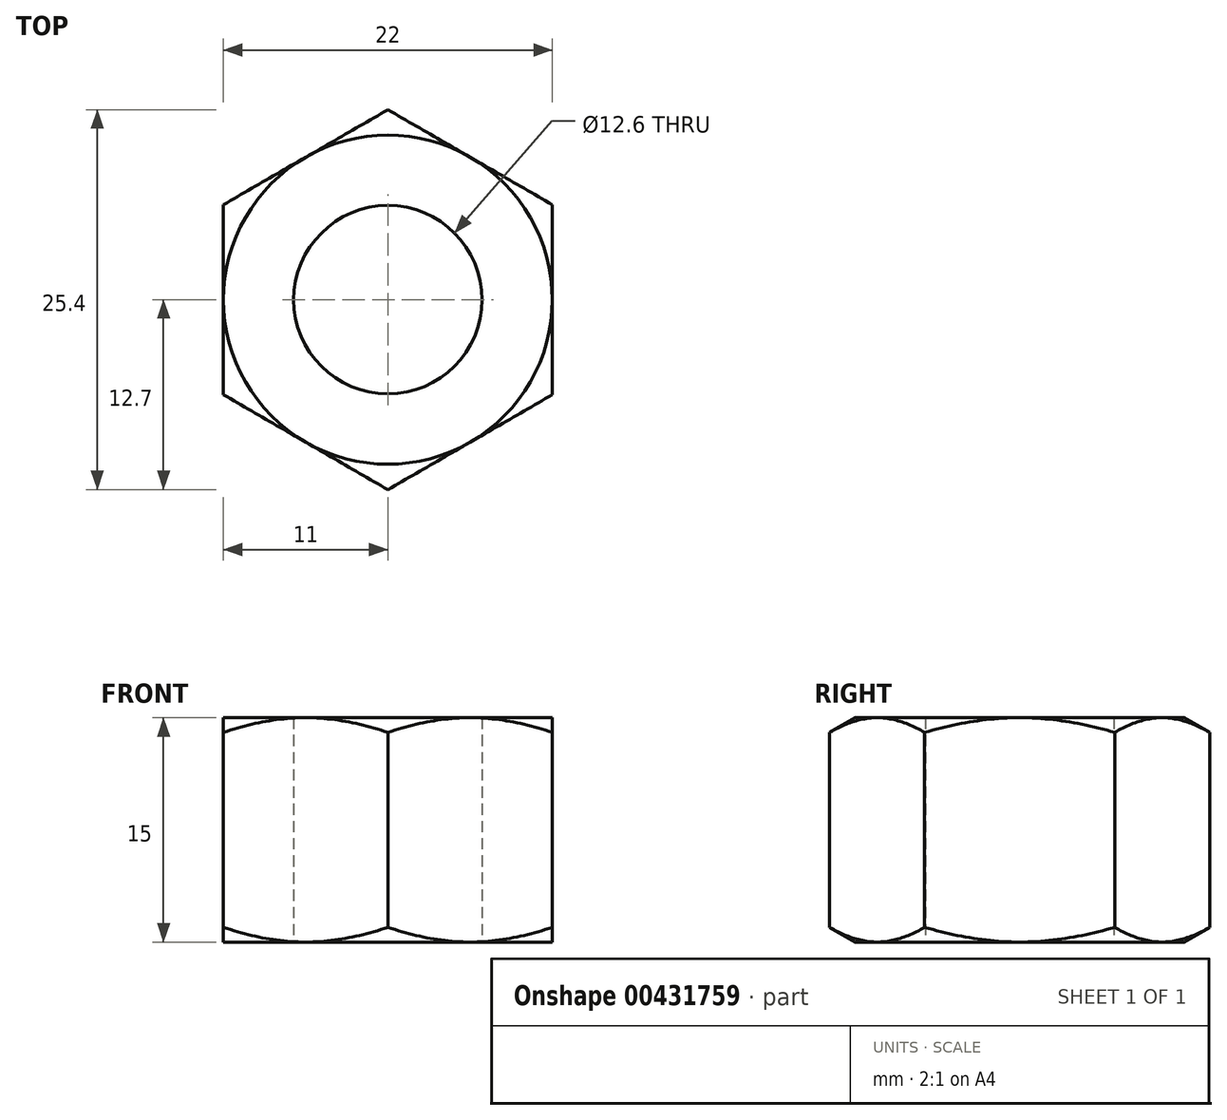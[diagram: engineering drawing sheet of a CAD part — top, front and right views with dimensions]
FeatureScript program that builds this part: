
annotation { "Feature Type Name" : "Feature", "Feature Type Description" : "" }
export const myFeature = defineFeature(function(context is Context, id is Id, definition is map)
    precondition{}
    {
        {
            var Q0;
            Q0=qCreatedBy(makeId("Top.planeOp"),FACE);
            var sketch = newSketch(context, id + "F0", { "sketchPlane" : qUnion([Q0])});
            skCircle(sketch, "E0.cCircle", {"center": v(0, 0) * mm, "radius": 11 * mm, "construction": true});
            skLineSegment(sketch, "E0.0", {"start": v(11, 6.35) * mm, "end": v(11, -6.35) * mm});
            skLineSegment(sketch, "E0.1", {"start": v(11, -6.35) * mm, "end": v(0, -12.7) * mm});
            skLineSegment(sketch, "E0.2", {"start": v(0, -12.7) * mm, "end": v(-11, -6.35) * mm});
            skLineSegment(sketch, "E0.3", {"start": v(-11, -6.35) * mm, "end": v(-11, 6.35) * mm});
            skLineSegment(sketch, "E0.4", {"start": v(-11, 6.35) * mm, "end": v(0, 12.7) * mm});
            skLineSegment(sketch, "E0.5", {"start": v(0, 12.7) * mm, "end": v(11, 6.35) * mm});
            skPoint(sketch, "E0.0.midPoint", {"position": v(11, 0) * mm});
            skCircle(sketch, "E1", {"center": v(0, 0) * mm, "radius": 6.3 * mm});
            skSolve(sketch);
        }
        {
            var Q0;
            Q0=makeQuery(id+"F0.imprint","IMPRINT",FACE,{"disambiguationData":[TD([[makeQuery(id+"F0.imprint","IMPRINT",EDGE,{"derivedFrom":sQuery(id+"F0.wireOp",EDGE,"E0.0")}),-1.0]])]});
            extrude(context, id + "F1", {"entities" : qUnion([Q0]), "depth" : 15 * mm});
        }
        {
            var Q0;
            Q0=qCreatedBy(makeId("Front.planeOp"),FACE);
            var sketch = newSketch(context, id + "F2", { "sketchPlane" : qUnion([Q0])});
            skLineSegment(sketch, "E2", {"start": v(11, 15) * mm, "end": v(17.64, 15) * mm});
            skLineSegment(sketch, "E3", {"start": v(17.64, 11.16) * mm, "end": v(11, 15) * mm});
            skLineSegment(sketch, "E4", {"start": v(17.64, 15) * mm, "end": v(17.64, 11.16) * mm});
            skLineSegment(sketch, "E5", {"start": v(34.82, 7.5) * mm, "end": v(-12.82, 7.5) * mm, "construction": true});
            skLineSegment(sketch, "E6.MirrorCS", {"start": v(11, 0) * mm, "end": v(17.64, 0) * mm});
            skLineSegment(sketch, "E7.MirrorCS", {"start": v(17.64, 3.84) * mm, "end": v(11, 0) * mm});
            skLineSegment(sketch, "E8.MirrorCS", {"start": v(17.64, 0) * mm, "end": v(17.64, 3.84) * mm});
            skLineSegment(sketch, "E9", {"start": v(0, 0) * mm, "end": v(0, 18.97) * mm, "construction": true});
            skSolve(sketch);
        }
        {
            var Q0;
            Q0=makeQuery(id+"F2.imprint","IMPRINT",FACE,{"disambiguationData":[TD([[makeQuery(id+"F2.imprint","IMPRINT",EDGE,{"derivedFrom":sQuery(id+"F2.wireOp",EDGE,"E2")}),-1.0]])]});
            var Q1;
            Q1=makeQuery(id+"F2.imprint","IMPRINT",FACE,{"disambiguationData":[TD([[makeQuery(id+"F2.imprint","IMPRINT",EDGE,{"derivedFrom":sQuery(id+"F2.wireOp",EDGE,"E6.MirrorCS")}),1.0]])]});
            var Q2;
            Q2=sQuery(id+"F2.wireOp",EDGE,"E9");
            revolve(context, id + "F3", {"operationType" : NewBodyOperationType.REMOVE, "entities" : qUnion([Q0, Q1]), "axis" : qUnion([Q2]), "revolveType" : RevolveType.FULL, "oppositeDirection" : true});
        }
    });
